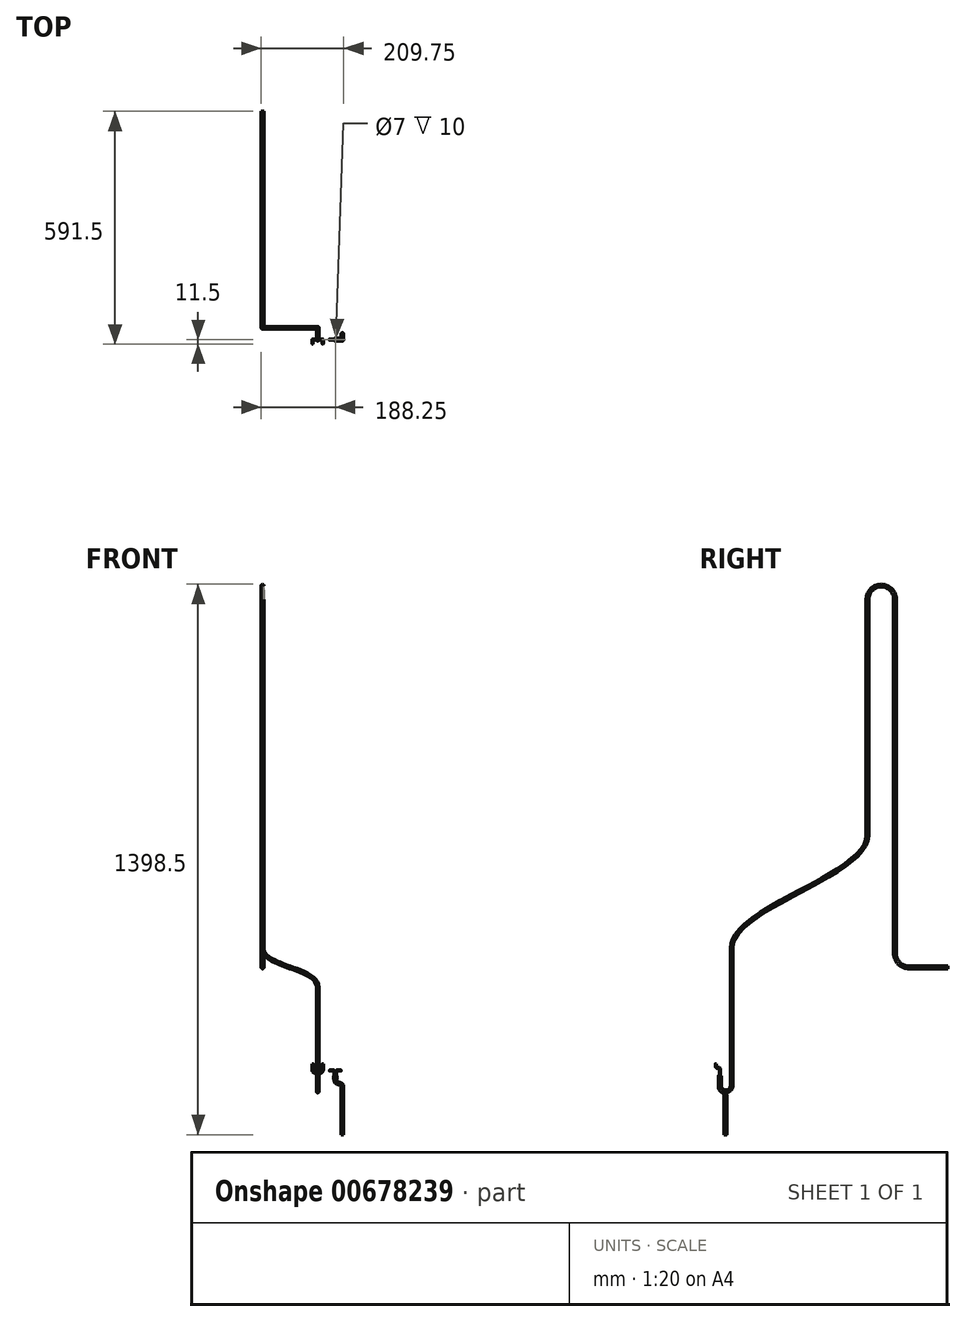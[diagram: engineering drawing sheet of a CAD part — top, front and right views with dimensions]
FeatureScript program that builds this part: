
annotation { "Feature Type Name" : "Feature", "Feature Type Description" : "" }
export const myFeature = defineFeature(function(context is Context, id is Id, definition is map)
    precondition{}
    {
        {
            var Q0;
            Q0=qCreatedBy(makeId("Top.planeOp"),FACE);
            var sketch = newSketch(context, id + "F0", { "sketchPlane" : qUnion([Q0])});
            skCircle(sketch, "E0", {"center": v(0, 0) * mm, "radius": 3.5 * mm});
            skSolve(sketch);
        }
        {
            var Q0;
            Q0=qCreatedBy(makeId("Front.planeOp"),FACE);
            var sketch = newSketch(context, id + "F1", { "sketchPlane" : qUnion([Q0])});
            skLineSegment(sketch, "E1", {"start": v(0, 0) * mm, "end": v(0, -10) * mm});
            skFitSpline(sketch, "E2", {"points": [v(0, -10) * mm, v(18, -30) * mm], "startDerivative": vector(0, -45) * mm, "endDerivative": vector(0, -45) * mm});
            skSolve(sketch);
        }
        {
            var Q0;
            Q0=qCreatedBy(makeId("Right.planeOp"),FACE);
            cPlane(context, id + "F2", {"entities" : qUnion([Q0]), "cplaneType" : CPlaneType.OFFSET, "offset" : 18 * mm, "width" : 150 * mm, "height" : 150 * mm});
        }
        {
            var Q0;
            Q0=qCreatedBy(id+"F2.planeOp",FACE);
            var sketch = newSketch(context, id + "F3", { "sketchPlane" : qUnion([Q0])});
            skFitSpline(sketch, "E3", {"points": [v(0, -30) * mm, v(14, -50) * mm], "startDerivative": vector(0, -30) * mm, "endDerivative": vector(0, -30) * mm});
            skLineSegment(sketch, "E4", {"start": v(14, -50) * mm, "end": v(14, -150) * mm});
            skSolve(sketch);
        }
        {
            var Q0;
            Q0=qSketchRegion(id+"F0",true);
            var Q1;
            Q1=qConstructionFilter(qBodyType(qCreatedBy(id+"F1",EDGE),BodyType.WIRE),ConstructionObject.NO);
            var Q2;
            Q2=qConstructionFilter(qBodyType(qCreatedBy(id+"F3",EDGE),BodyType.WIRE),ConstructionObject.NO);
            sweep(context, id + "F4", {"profiles" : qUnion([Q0]), "path" : qUnion([Q1, Q2])});
        }
        {
            var Q0;
            Q0=makeQuery(id+"F4.opSweep","CAP_FACE",FACE,{"disambiguationData":[OSD([sQuery(id+"F0.wireOp",EDGE,"E0"),sQuery(id+"F1.wireOp",VERTEX,"E1.start")])],"isStart":true});
            var sketch = newSketch(context, id + "F5", { "sketchPlane" : qUnion([Q0])});
            skCircle(sketch, "E5", {"center": v(1.5, 0) * mm, "radius": 1.5 * mm});
            skSolve(sketch);
        }
        {
            var Q0;
            Q0=qCreatedBy(makeId("Front.planeOp"),FACE);
            var sketch = newSketch(context, id + "F6", { "sketchPlane" : qUnion([Q0])});
            skFitSpline(sketch, "E6", {"points": [v(1.5, 0) * mm, v(2, 5) * mm], "startDerivative": vector(0, 9) * mm, "endDerivative": vector(0, 9) * mm});
            skLineSegment(sketch, "E7", {"start": v(2, 5) * mm, "end": v(2, 10) * mm});
            skArc(sketch, "E8", {"start": v(5, 13) * mm, "mid": v(2.88, 12.12) * mm, "end": v(2, 10) * mm});
            skLineSegment(sketch, "E9", {"start": v(5, 13) * mm, "end": v(15, 13) * mm});
            skSolve(sketch);
        }
        {
            var Q0;
            Q0=qSketchRegion(id+"F5",true);
            var Q1;
            Q1=qConstructionFilter(qBodyType(qCreatedBy(id+"F6",EDGE),BodyType.WIRE),ConstructionObject.NO);
            sweep(context, id + "F7", {"profiles" : qUnion([Q0]), "path" : qUnion([Q1])});
        }
        {
            var Q0;
            Q0=makeQuery(id+"F7.opSweep","SWEPT_BODY",BODY,{"disambiguationData":[OSD([sQuery(id+"F5.wireOp",EDGE,"E5"),sQuery(id+"F6.wireOp",EDGE,"E7")])]});
            var Q1;
            Q1=qCreatedBy(makeId("Right.planeOp"),FACE);
            mirror(context, id + "F8", {"entities" : qUnion([Q0]), "mirrorPlane" : qUnion([Q1])});
        }
        {
            var Q0;
            Q0=makeQuery(id+"F4.opSweep","CAP_FACE",FACE,{"disambiguationData":[OSD([sQuery(id+"F0.wireOp",EDGE,"E0"),sQuery(id+"F1.wireOp",VERTEX,"E1.start")])],"isStart":true});
            var sketch = newSketch(context, id + "F9", { "sketchPlane" : qUnion([Q0])});
            skCircle(sketch, "E10.0", {"center": v(0, 0) * mm, "radius": 3.5 * mm});
            skCircle(sketch, "E11.0", {"center": v(0, 0) * mm, "radius": 4 * mm});
            skSolve(sketch);
        }
        {
            var Q0;
            Q0=qSketchRegion(id+"F9",true);
            extrude(context, id + "F10", {"entities" : qUnion([Q0]), "oppositeDirection" : true, "depth" : 10 * mm, "offsetDistance" : 25 * mm});
        }
        {
            var Q0;
            Q0=qCreatedBy(makeId("Top.planeOp"),FACE);
            var sketch = newSketch(context, id + "F11", { "sketchPlane" : qUnion([Q0])});
            skCircle(sketch, "E12", {"center": v(-44.75, 0) * mm, "radius": 3.5 * mm});
            skSolve(sketch);
        }
        {
            var Q0;
            Q0=qSketchRegion(id+"F11",true);
            extrude(context, id + "F12", {"entities" : qUnion([Q0]), "oppositeDirection" : true, "depth" : 25 * mm, "offsetDistance" : 25 * mm});
        }
        {
            var Q0;
            Q0=makeQuery(id+"F12.opExtrude","CAP_FACE",FACE,{"disambiguationData":[OSD([sQuery(id+"F11.wireOp",EDGE,"E12")])],"isStart":true});
            var sketch = newSketch(context, id + "F13", { "sketchPlane" : qUnion([Q0])});
            skCircle(sketch, "E13", {"center": v(-43.25, 0) * mm, "radius": 1.5 * mm});
            skPoint(sketch, "E14", {"position": v(-44.75, 0) * mm});
            skSolve(sketch);
        }
        {
            var Q0;
            Q0=qCreatedBy(makeId("Front.planeOp"),FACE);
            var sketch = newSketch(context, id + "F14", { "sketchPlane" : qUnion([Q0])});
            skFitSpline(sketch, "E15", {"points": [v(-43.25, 0) * mm, v(-37.5, 7.5) * mm, v(-31.75, 15) * mm], "startDerivative": vector(0, 30) * mm, "endDerivative": vector(0, 30) * mm});
            skLineSegment(sketch, "E16", {"start": v(-43.25, 5) * mm, "end": v(-43.25, 0) * mm, "construction": true});
            skLineSegment(sketch, "E17", {"start": v(-31.75, 15) * mm, "end": v(-31.75, 10) * mm, "construction": true});
            skLineSegment(sketch, "E18", {"start": v(-31.75, 15) * mm, "end": v(-43.25, 0) * mm, "construction": true});
            skSolve(sketch);
        }
        {
            var Q0;
            Q0=qCreatedBy(makeId("Right.planeOp"),FACE);
            var Q1;
            Q1=sQuery(id+"F14.wireOp",VERTEX,"E18.start");
            cPlane(context, id + "F15", {"entities" : qUnion([Q0, Q1]), "cplaneType" : CPlaneType.PLANE_POINT, "offset" : 25 * mm, "width" : 150 * mm, "height" : 150 * mm});
        }
        {
            var Q0;
            Q0=qCreatedBy(id+"F15.planeOp",FACE);
            var sketch = newSketch(context, id + "F16", { "sketchPlane" : qUnion([Q0])});
            skFitSpline(sketch, "E19", {"points": [v(0, 15) * mm, v(-5, 20) * mm, v(-10, 25) * mm], "startDerivative": vector(0, 30) * mm, "endDerivative": vector(0, 30) * mm});
            skLineSegment(sketch, "E20", {"start": v(-10, 20) * mm, "end": v(-10, 25) * mm, "construction": true});
            skLineSegment(sketch, "E21", {"start": v(0, 20) * mm, "end": v(0, 15) * mm, "construction": true});
            skLineSegment(sketch, "E22", {"start": v(0, 15) * mm, "end": v(-10, 25) * mm, "construction": true});
            skLineSegment(sketch, "E23", {"start": v(-10, 25) * mm, "end": v(-10, 30) * mm});
            skSolve(sketch);
        }
        {
            var Q0;
            Q0=makeQuery(id+"F13.imprint","IMPRINT",FACE,{"disambiguationData":[TD([[makeQuery(id+"F13.imprint","IMPRINT",EDGE,{"derivedFrom":sQuery(id+"F13.wireOp",EDGE,"E13")}),1.0]])]});
            var Q1;
            Q1=sQuery(id+"F16.wireOp",EDGE,"E19");
            var Q2;
            Q2=sQuery(id+"F14.wireOp",EDGE,"E15");
            var Q3;
            Q3=sQuery(id+"F16.wireOp",EDGE,"E23");
            sweep(context, id + "F17", {"profiles" : qUnion([Q0]), "path" : qUnion([Q1, Q2, Q3])});
        }
        {
            var Q0;
            Q0=qCreatedBy(makeId("Right.planeOp"),FACE);
            var Q1;
            Q1=sQuery(id+"F13.wireOp",VERTEX,"E14");
            cPlane(context, id + "F18", {"entities" : qUnion([Q0, Q1]), "cplaneType" : CPlaneType.PLANE_POINT, "offset" : 25 * mm, "width" : 150 * mm, "height" : 150 * mm});
        }
        {
            var Q0;
            Q0=makeQuery(id+"F17.opSweep","SWEPT_BODY",BODY,{"disambiguationData":[OSD([sQuery(id+"F13.wireOp",EDGE,"E13"),sQuery(id+"F14.wireOp",EDGE,"E15")])]});
            var Q1;
            Q1=qCreatedBy(id+"F18.planeOp",FACE);
            mirror(context, id + "F19", {"entities" : qUnion([Q0]), "mirrorPlane" : qUnion([Q1])});
        }
        {
            var Q0;
            Q0=qCreatedBy(id+"F18.planeOp",FACE);
            var sketch = newSketch(context, id + "F20", { "sketchPlane" : qUnion([Q0])});
            skArc(sketch, "E24", {"start": v(0, -25) * mm, "mid": v(15, -40) * mm, "end": v(30, -25) * mm});
            skLineSegment(sketch, "E25", {"start": v(30, -25) * mm, "end": v(30, 225) * mm});
            skSolve(sketch);
        }
        {
            var Q0;
            Q0=qCreatedBy(makeId("Front.planeOp"),FACE);
            var Q1;
            Q1=sQuery(id+"F20.wireOp",VERTEX,"E25.end");
            cPlane(context, id + "F21", {"entities" : qUnion([Q0, Q1]), "cplaneType" : CPlaneType.PLANE_POINT, "offset" : 25 * mm, "width" : 150 * mm, "height" : 150 * mm});
        }
        {
            var Q0;
            Q0=qCreatedBy(id+"F21.planeOp",FACE);
            var sketch = newSketch(context, id + "F22", { "sketchPlane" : qUnion([Q0])});
            skFitSpline(sketch, "E26", {"points": [v(-44.75, 225) * mm, v(-114.75, 275) * mm, v(-184.75, 325) * mm], "startDerivative": vector(0, 150) * mm, "endDerivative": vector(0, 150) * mm});
            skLineSegment(sketch, "E27", {"start": v(-44.75, 225) * mm, "end": v(-184.75, 325) * mm, "construction": true});
            skLineSegment(sketch, "E28", {"start": v(-184.75, 325) * mm, "end": v(-184.75, 300) * mm, "construction": true});
            skLineSegment(sketch, "E29", {"start": v(-44.75, 250) * mm, "end": v(-44.75, 225) * mm, "construction": true});
            skSolve(sketch);
        }
        {
            var Q0;
            Q0=qCreatedBy(makeId("Right.planeOp"),FACE);
            var Q1;
            Q1=sQuery(id+"F22.wireOp",VERTEX,"E26.2.internal");
            cPlane(context, id + "F23", {"entities" : qUnion([Q0, Q1]), "cplaneType" : CPlaneType.PLANE_POINT, "offset" : 25 * mm, "width" : 150 * mm, "height" : 150 * mm});
        }
        {
            var Q0;
            Q0=qCreatedBy(id+"F23.planeOp",FACE);
            var sketch = newSketch(context, id + "F24", { "sketchPlane" : qUnion([Q0])});
            skFitSpline(sketch, "E30", {"points": [v(30, 325) * mm, v(202.5, 467.5) * mm, v(375, 610) * mm], "startDerivative": vector(0, 300) * mm, "endDerivative": vector(0, 300) * mm});
            skLineSegment(sketch, "E31", {"start": v(375, 560) * mm, "end": v(375, 610) * mm, "construction": true});
            skLineSegment(sketch, "E32", {"start": v(375, 610) * mm, "end": v(30, 325) * mm, "construction": true});
            skLineSegment(sketch, "E33", {"start": v(30, 375) * mm, "end": v(30, 325) * mm, "construction": true});
            skLineSegment(sketch, "E34", {"start": v(375, 610) * mm, "end": v(375, 1210) * mm});
            skArc(sketch, "E35", {"start": v(445, 1210) * mm, "mid": v(410, 1245) * mm, "end": v(375, 1210) * mm});
            skLineSegment(sketch, "E36", {"start": v(445, 1210) * mm, "end": v(445, 310) * mm});
            skArc(sketch, "E37", {"start": v(445, 310) * mm, "mid": v(455.25, 285.25) * mm, "end": v(480, 275) * mm});
            skLineSegment(sketch, "E38", {"start": v(480, 275) * mm, "end": v(580, 275) * mm});
            skSolve(sketch);
        }
        {
            var Q0;
            Q0=makeQuery(id+"F12.opExtrude","CAP_FACE",FACE,{"disambiguationData":[OSD([sQuery(id+"F11.wireOp",EDGE,"E12")])],"isStart":false});
            var Q1;
            Q1=qConstructionFilter(qBodyType(qCreatedBy(id+"F20",EDGE),BodyType.WIRE),ConstructionObject.NO);
            var Q2;
            Q2=qConstructionFilter(qBodyType(qCreatedBy(id+"F22",EDGE),BodyType.WIRE),ConstructionObject.NO);
            var Q3;
            Q3=qConstructionFilter(qBodyType(qCreatedBy(id+"F24",EDGE),BodyType.WIRE),ConstructionObject.NO);
            sweep(context, id + "F25", {"operationType" : NewBodyOperationType.ADD, "profiles" : qUnion([Q0]), "path" : qUnion([Q1, Q2, Q3])});
        }
    });
